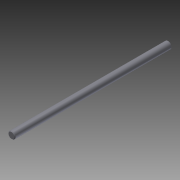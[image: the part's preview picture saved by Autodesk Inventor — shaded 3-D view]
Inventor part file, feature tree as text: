
AUTODESK INVENTOR PART (.ipt)
format: ipt  version: 2013 (Build 170138000, 138)  size: 69,632 bytes
history: native  units: in
note: dims shown in document units (in); Inventor stores cm internally (conversion verified against a paired STEP export)
features: extrude x1, chamfer x1, sketch x1
ambient origin geometry x8: Origin, YZ Plane, XZ Plane, XY Plane, X Axis, Y Axis, Z Axis, Center Point
bodies: Solid1 (feature_tree)
feature tree (3):
  extrude  "Extrusion1"  Depth=1.299in TaperAngle=0.0deg
  chamfer  "Chamfer1"  Distance=0.005in Angle=45.0deg
  sketch  "Sketch1"  dims[d0=0.059in d1=1.299in d2=0.0in d3=0.005in d4=0.125in d5=45.0deg]
